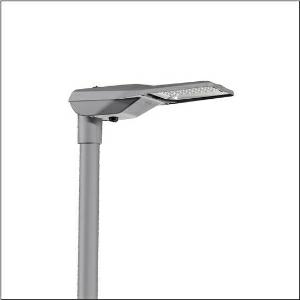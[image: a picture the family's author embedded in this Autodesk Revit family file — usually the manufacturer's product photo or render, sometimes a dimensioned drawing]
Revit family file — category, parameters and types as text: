
# Revit family: streetlight_sl_21_iq_mini___p0_5a_5xe2v31y08gb_32b4
name_source: partatom
category: Lighting Fixtures
units: mm (PartAtom-declared; Revit-internal decimal feet)

## family parameters
Cut with Voids When Loaded = No
Host = Face
Light Source = No
Part Type = Normal
Room Calculation Point = No
Round Connector Dimension = Use Diameter
Shared = No

## types (1)
- --- (1 x LED, 5880 lm, 39.8 W, 3000K)
    Apparent Load = 40 VA
    CIE Flux Codes = 37 73 96 100 100
    Color Rendering = 70
    Color Temperature = 3000K
    Default Elevation = 1800 mm
    Description = Streetlight SL 21 iQ mini, mast luminaire, primary light control with lens, of PMMA, primary optical cover: cover, of toughened safety glass, transparent, light distribution: P0.5a, light emission: direct distribution, primary light characteristic: asymmetric, installation type: post-top, side-entry, LED, High Power LED, rated luminous flux: 5.880lm, luminous efficacy: 148lm/W, light colour: 730, colour temperature: 3000K, control gear: iQ-Street Remote, D4i with power reduction, control: pre-setting: logarithmic dimming characteristic, Street-Remote, Auto-Match, Temp-Guard, Lumen-Switch, Night-Set, Smart-Wire, Light-Fading, Desk-Remote (wireless, voltage-free reading and setting of iQ features in the workshop via application-optimized NFC function/RFID function), optimised constant luminous flux control (CLO 2.0), mains connection: 220..240V, AC, 50/60Hz, start of lifetime: 40W, end of service life: 41W, reduction: 18W, luminaire housing, of diecast aluminium, powder-coated, Siteco® metallic grey (DB 702S), corrosivity category C5 mid according to DIN EN ISO 12944, please order mast flange separately, inclination adjustable: 0°, 5°, 10°, 15°, sealing non-destructively replaceable, multi-level sealing system, length: 628mm, width: 235mm, height: 110mm, mast flange for spigot size: 42mm (side-entry): 5XC10008XM4, 60/48mm (side-entry/post-top): 5XC10108XM2, 76/60mm (side-entry/post-top): 5XC10108XM1, mounting height: 4..8m, Smart Interface below and above, protection rating (complete): IP66, insulation class (complete): insulation class II (safety insulation), certification: CE, ENEC, ENEC+, VDE, impact resistance: IK10, permissible operating ambient temperature for outdoor applications: -40..+50°C, standard-compliant lighting for roads and squares, packaging unit: 1 piece

Light Distribution: P0.5a
    Height = 110 mm
    Lamp = 1 x LED
    Lamp Light Flux = 5880 lm
    Lamp Power = 39.8 W
    Lamp count = 1
    Length = 625 mm
    Luminous efficacy = 148 lm/W
    Manufacturer = Siteco
    ModVariant = No
    Model = 5XE2V31Y08GB
    Number of Poles = 1
    OnlyDefault = Yes
    Power Factor = 1
    Product Name = Streetlight SL 21 iQ mini | P0.5a
    Product group = mast luminaire | pylon top
    ProductGroupID = 6100
    Protection Class = Protection class II
    Protection Degree = IP 66
    RLX_Detail_Level = 1
    RLX_Emergency_Light_Flux = 0 lm
    RLX_Emergency_Type = 0
    RLX_Emergency_Type_DB = No
    RlxData = <blob elided: 26377 chars, md5=b9713160>
    Socket = socket
    Standby Power = 0 W
    System Light Flux = 5880 lm
    System Power = 40 W
    Type Comments = factory setting: luminous flux: 100 % | dim-lin: 254 | 800 mA
    Type Image = l_1003514.jpg
    URL = http://relux.com
    VarID = @adj_070594
    Voltage = 0 V
    Weight = 0.00 kg
    Width = 234 mm

## geometry (parser evidence)
native form markers: Blend x4, Sweep x11
no freeform markers — native parametric forms only
